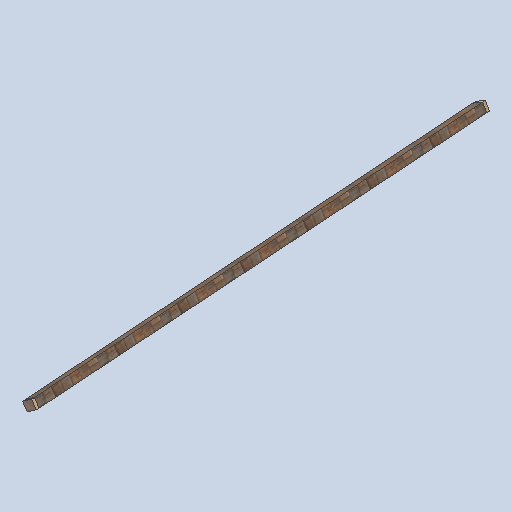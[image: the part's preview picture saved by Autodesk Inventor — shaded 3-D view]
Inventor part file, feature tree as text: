
AUTODESK INVENTOR PART (.ipt)
format: ipt  version: 2024.2 (Build 282272000, 272)  size: 134,656 bytes
history: native  units: in
note: dims shown in document units (in); Inventor stores cm internally (conversion verified against a paired STEP export)
features: sketch x4, other x3, plane x2
ambient origin geometry x8: Origin, YZ Plane, XZ Plane, XY Plane, X Axis, Y Axis, Z Axis, Center Point
bodies: Solid1 (feature_tree)
feature tree (9):
  other  "support_beam_segment_0103.ipt"
  other  "Solid1::support_beam_segment_0103.ipt"
  other  "TaggingFeature1"
  sketch  "Sketch1"  dims[d0=0.3937in]
  sketch  "Sketch2"
  sketch  "Sketch3"
  sketch  "Sketch4"
  plane  "Work Plane1"
  plane  "Work Plane2"
